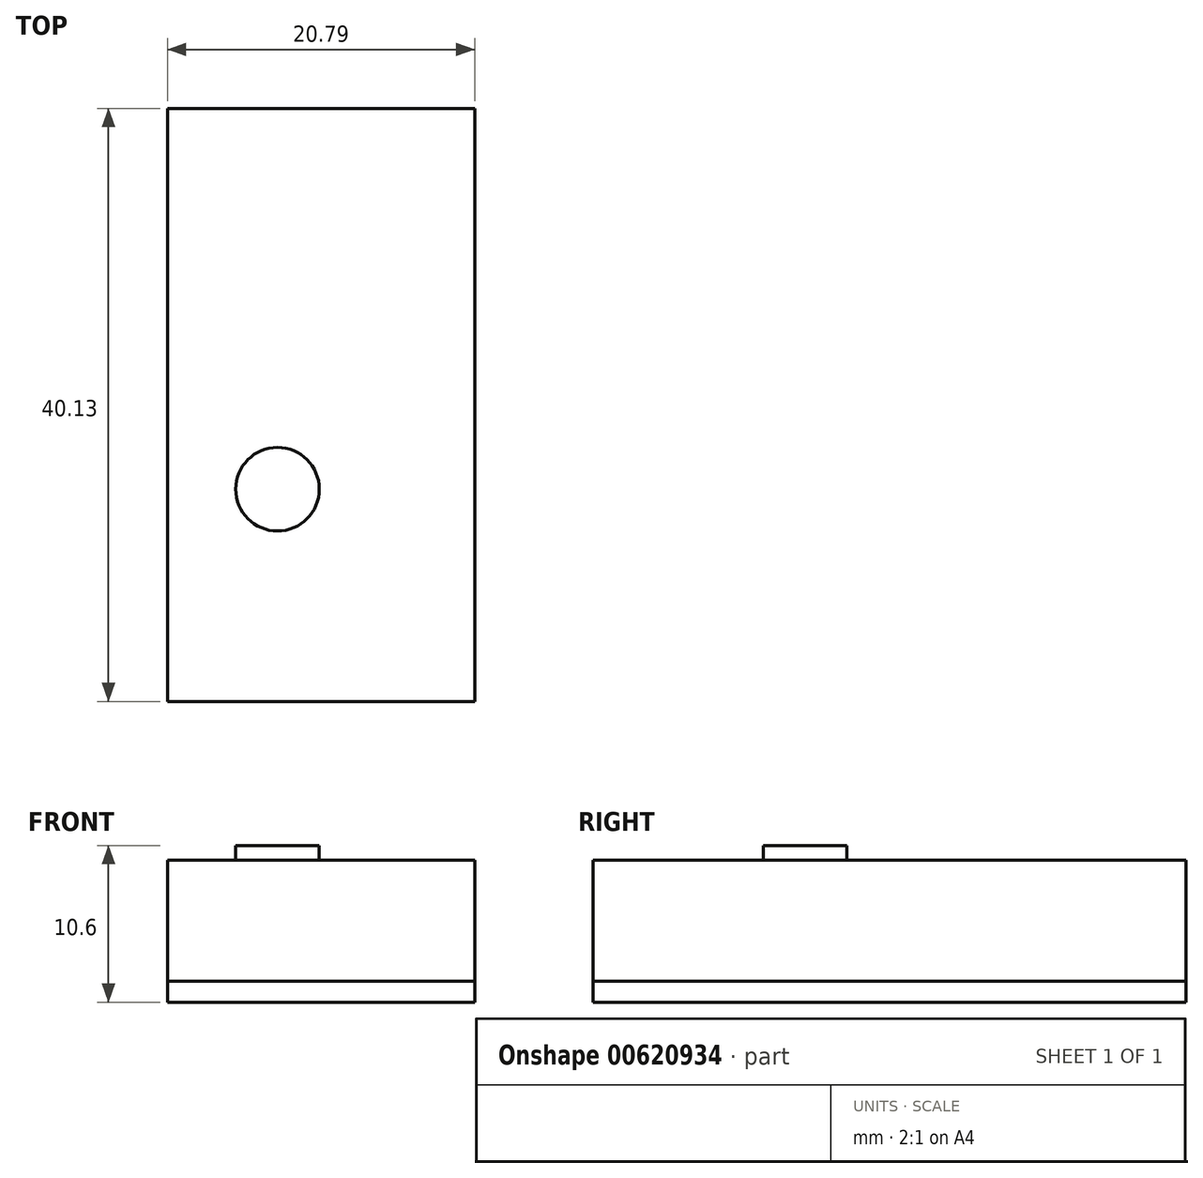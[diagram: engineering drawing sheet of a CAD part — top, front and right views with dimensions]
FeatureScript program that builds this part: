
annotation { "Feature Type Name" : "Feature", "Feature Type Description" : "" }
export const myFeature = defineFeature(function(context is Context, id is Id, definition is map)
    precondition{}
    {
        {
            var Q0;
            Q0=qCreatedBy(makeId("Front.planeOp"),FACE);
            var sketch = newSketch(context, id + "F0", { "sketchPlane" : qUnion([Q0])});
            skLineSegment(sketch, "E0.bottom", {"start": v(-49.72, 55.97) * mm, "end": v(-28.93, 55.97) * mm});
            skLineSegment(sketch, "E0.top", {"start": v(-49.72, 47.8) * mm, "end": v(-28.93, 47.8) * mm});
            skLineSegment(sketch, "E0.left", {"start": v(-49.72, 55.97) * mm, "end": v(-49.72, 47.8) * mm});
            skLineSegment(sketch, "E0.right", {"start": v(-28.93, 55.97) * mm, "end": v(-28.93, 47.8) * mm});
            skPoint(sketch, "E0.middle", {"position": v(-39.32, 51.88) * mm});
            skSolve(sketch);
        }
        {
            var Q0;
            Q0=makeQuery(id+"F0.imprint","IMPRINT",FACE,{"disambiguationData":[TD([[makeQuery(id+"F0.imprint","IMPRINT",EDGE,{"derivedFrom":sQuery(id+"F0.wireOp",EDGE,"E0.bottom")}),-1.0]])]});
            extrude(context, id + "F1", {"entities" : qUnion([Q0]), "depth" : 40.13 * mm, "offsetDistance" : 25.4 * mm});
        }
        {
            var Q0;
            Q0=makeQuery(id+"F1.opExtrude","SWEPT_FACE",FACE,{"disambiguationData":[OSD([sQuery(id+"F0.wireOp",EDGE,"E0.bottom")])]});
            extrude(context, id + "F2", {"entities" : qUnion([Q0]), "oppositeDirection" : true, "depth" : 9.6 * mm, "offsetDistance" : 25 * mm});
        }
        {
            var Q0;
            Q0=makeQuery(id+"F1.opExtrude","SWEPT_FACE",FACE,{"disambiguationData":[OSD([sQuery(id+"F0.wireOp",EDGE,"E0.bottom")])]});
            var sketch = newSketch(context, id + "F3", { "sketchPlane" : qUnion([Q0])});
            skCircle(sketch, "E1", {"center": v(-42.28, -25.77) * mm, "radius": 2.83 * mm});
            skSolve(sketch);
        }
        {
            var Q0;
            Q0=makeQuery(id+"F3.imprint","IMPRINT",FACE,{"disambiguationData":[TD([[makeQuery(id+"F3.imprint","IMPRINT",EDGE,{"derivedFrom":sQuery(id+"F3.wireOp",EDGE,"E1")}),1.0]])]});
            extrude(context, id + "F4", {"entities" : qUnion([Q0]), "depth" : 1 * mm, "offsetDistance" : 25 * mm});
        }
    });
